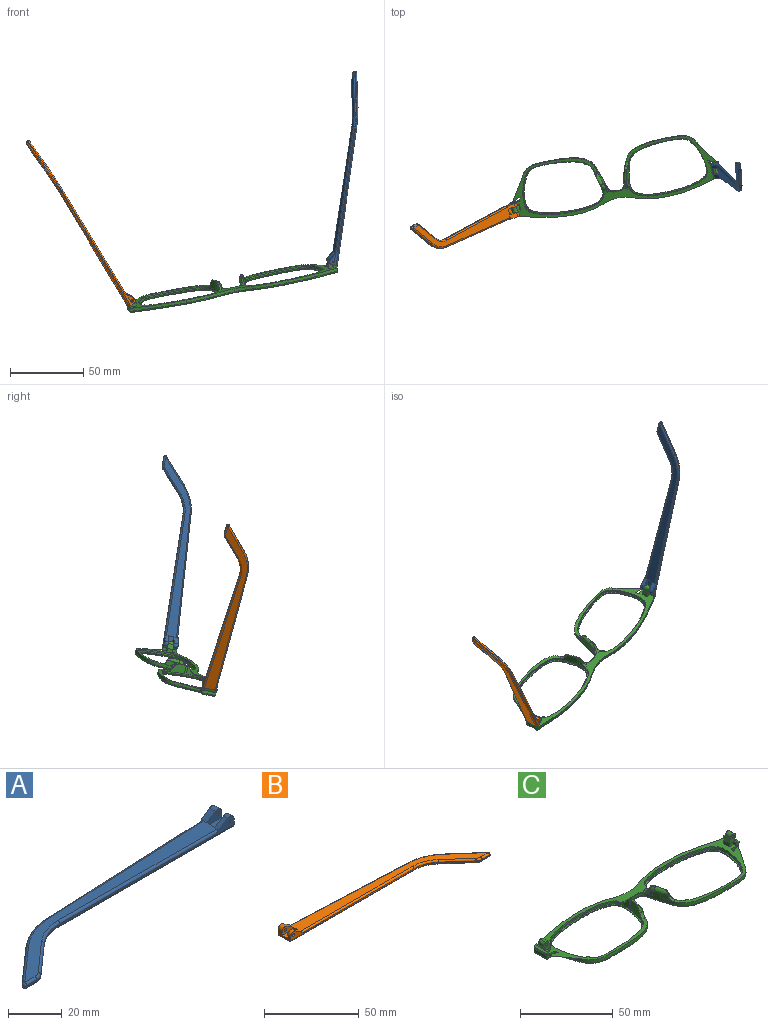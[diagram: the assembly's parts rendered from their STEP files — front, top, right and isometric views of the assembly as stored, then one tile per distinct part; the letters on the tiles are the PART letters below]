
ASSEMBLY  parts=3 mates=2
PART A: 43 faces, bbox 130.2x29.5x5.9 mm
  f0: plane 9.62x3.72mm, normal (1,0,0), area 24.7mm2, adj f1,f3,f4,f5,f10,f16,f18,f28
  f1: cylinder r=2.2mm len=3.45mm, axis (0,-1,0), area 11mm2, adj f0,f2,f4,f37
  f2: plane 6.01x3.91mm, normal (-0.55,0,0.84), area 12.7mm2, adj f1,f4,f9,f19,f37
  f3: plane 2.26x0.1mm, normal (0,0,1), area 0.1mm2, adj f0,f5,f18
  f4: plane 92.1x4.9mm, normal (0,-1,0), area 79.9mm2, adj f0,f1,f2,f14,f19,f36,f42
  f5: plane 93.42x4.13mm, normal (-0.04,1,0), area 64.8mm2, adj f0,f3,f11,f15,f17,f27,f28
  f6: plane 17.82x15.72mm, normal (-0.66,0.75,0), area 14.3mm2, adj f11,f12,f25,f30
  f7: plane 5.46x0.6mm, normal (0,-1,0), area 3.3mm2, adj f12,f13,f23,f32
  f8: plane 14.99x13.23mm, normal (0.66,-0.75,0), area 12mm2, adj f13,f14,f21,f34
  f9: plane 121.18x26.73mm, normal (0,0,1), area 627.7mm2, adj f2,f17,f19,f20,f21,f22,f23,f25
  f10: plane 129.1x27.08mm, normal (0,0,-1), area 686.5mm2, adj f0,f28,f29,f30,f32,f33,f34,f35
  f11: cylinder r=30mm len=18.52mm, axis (0,0,-1), area 12.2mm2, adj f5,f6,f26,f29
  f12: cylinder r=1mm len=1.75mm, axis (0,0,-1), area 1.5mm2, adj f6,f7,f24,f31
  f13: cylinder r=5mm len=3.31mm, axis (0,0,-1), area 2.2mm2, adj f7,f8,f22,f33
  f14: cylinder r=20mm len=13.23mm, axis (0,0,1), area 8.7mm2, adj f4,f8,f20,f35
  f15: plane 5.66x0.25mm, normal (0,0,-1), area 0.7mm2, adj f5,f17,f18
  f16: cylinder r=2.2mm len=3.45mm, axis (0,-1,0), area 14.8mm2, adj f0,f17,f18,f38
  f17: plane 6.01x3.91mm, normal (-0.55,0,0.84), area 16.9mm2, adj f5,f9,f15,f16,f18,f27,f38
  f18: plane 7.92x3.3mm, normal (0,1,0), area 15.9mm2, adj f0,f3,f15,f16,f17,f41
  f19: cylinder r=1mm len=84.18mm, axis (-1,0,0), area 131.4mm2, adj f2,f4,f9,f20
  f20: torus R=21mm, axis (0,0,1), area 23.1mm2, adj f9,f14,f19,f21
  f21: cylinder r=1mm len=15.65mm, axis (-0.75,-0.66,0), area 31.4mm2, adj f8,f9,f20,f22
  f22: torus R=4mm, axis (0,0,1), area 5.3mm2, adj f9,f13,f21,f23
  f23: cylinder r=1mm len=5.46mm, axis (-1,0,0), area 8.6mm2, adj f7,f9,f22,f24
  f24: sphere r=1mm, area 2.4mm2, adj f12,f23,f25
  f25: cylinder r=1mm len=18.48mm, axis (0.75,0.66,0), area 37.3mm2, adj f6,f9,f24,f26
  f26: torus R=29mm, axis (0,0,1), area 31.6mm2, adj f9,f11,f25,f27
  f27: cylinder r=1mm len=85.5mm, axis (1,0.04,0), area 133.5mm2, adj f5,f9,f17,f26
  f28: cylinder r=1mm len=93.46mm, axis (-1,-0.04,0), area 146.9mm2, adj f0,f5,f10,f29
  f29: torus R=29mm, axis (0,0,1), area 31.6mm2, adj f10,f11,f28,f30
  f30: cylinder r=1mm len=18.48mm, axis (-0.75,-0.66,0), area 37.3mm2, adj f6,f10,f29,f31
  f31: sphere r=1mm, area 2.4mm2, adj f12,f30,f32
  f32: cylinder r=1mm len=5.46mm, axis (1,0,0), area 8.6mm2, adj f7,f10,f31,f33
  f33: torus R=4mm, axis (0,0,1), area 5.3mm2, adj f10,f13,f32,f34
  f34: cylinder r=1mm len=15.65mm, axis (0.75,0.66,0), area 31.4mm2, adj f8,f10,f33,f35
  f35: torus R=21mm, axis (0,0,1), area 23.1mm2, adj f10,f14,f34,f36
  f36: cylinder r=1mm len=92.1mm, axis (1,0,0), area 144.7mm2, adj f0,f4,f10,f35
  f37: plane 7.92x4.7mm, normal (0,1,0), area 27mm2, adj f0,f1,f2,f39,f40,f42
  f38: plane 7.92x4.7mm, normal (0,-1,0), area 27mm2, adj f0,f16,f17,f39,f40,f41
  f39: plane 7.92x4.1mm, normal (0,0,1), area 32.5mm2, adj f0,f37,f38,f40
  f40: plane 4.1x1.4mm, normal (1,0,0), area 5.7mm2, adj f9,f37,f38,f39
  f41: cylinder r=0.5mm len=3.1mm, axis (0,-1,0), area 9.7mm2, adj f18,f38
  f42: cylinder r=0.5mm len=2.3mm, axis (0,-1,0), area 7.2mm2, adj f4,f37
PART B: 43 faces, bbox 130.2x29.5x5.9 mm
  f0: plane 9.62x3.72mm, normal (-1,0,0), area 24.7mm2, adj f1,f3,f4,f5,f10,f16,f18,f28
  f1: cylinder r=2.2mm len=3.45mm, axis (0,-1,0), area 11mm2, adj f0,f2,f4,f37
  f2: plane 6.01x3.91mm, normal (0.55,0,0.84), area 12.7mm2, adj f1,f4,f9,f19,f37
  f3: plane 2.26x0.1mm, normal (0,0,1), area 0.1mm2, adj f0,f5,f18
  f4: plane 92.1x4.9mm, normal (0,-1,0), area 78.2mm2, adj f0,f1,f2,f14,f19,f36,f42
  f5: plane 93.42x4.13mm, normal (0.04,1,0), area 64.8mm2, adj f0,f3,f11,f15,f17,f27,f28
  f6: plane 17.82x15.72mm, normal (0.66,0.75,0), area 14.3mm2, adj f11,f12,f25,f30
  f7: plane 5.46x0.6mm, normal (0,-1,0), area 3.3mm2, adj f12,f13,f23,f32
  f8: plane 14.99x13.23mm, normal (-0.66,-0.75,0), area 12mm2, adj f13,f14,f21,f34
  f9: plane 121.18x26.73mm, normal (0,0,1), area 627.7mm2, adj f2,f17,f19,f20,f21,f22,f23,f25
  f10: plane 129.1x27.08mm, normal (0,0,-1), area 686.5mm2, adj f0,f28,f29,f30,f32,f33,f34,f35
  f11: cylinder r=30mm len=18.52mm, axis (0,0,-1), area 12.2mm2, adj f5,f6,f26,f29
  f12: cylinder r=1mm len=1.75mm, axis (0,0,-1), area 1.5mm2, adj f6,f7,f24,f31
  f13: cylinder r=5mm len=3.31mm, axis (0,0,-1), area 2.2mm2, adj f7,f8,f22,f33
  f14: cylinder r=20mm len=13.23mm, axis (0,0,1), area 8.7mm2, adj f4,f8,f20,f35
  f15: plane 5.66x0.25mm, normal (0,0,-1), area 0.7mm2, adj f5,f17,f18
  f16: cylinder r=2.2mm len=3.45mm, axis (0,-1,0), area 14.8mm2, adj f0,f17,f18,f38
  f17: plane 6.01x3.91mm, normal (0.55,0,0.84), area 16.9mm2, adj f5,f9,f15,f16,f18,f27,f38
  f18: plane 7.92x3.3mm, normal (0,1,0), area 14.3mm2, adj f0,f3,f15,f16,f17,f41
  f19: cylinder r=1mm len=84.18mm, axis (1,0,0), area 131.4mm2, adj f2,f4,f9,f20
  f20: torus R=21mm, axis (0,0,1), area 23.1mm2, adj f9,f14,f19,f21
  f21: cylinder r=1mm len=15.65mm, axis (0.75,-0.66,0), area 31.4mm2, adj f8,f9,f20,f22
  f22: torus R=4mm, axis (0,0,1), area 5.3mm2, adj f9,f13,f21,f23
  f23: cylinder r=1mm len=5.46mm, axis (1,0,0), area 8.6mm2, adj f7,f9,f22,f24
  f24: sphere r=1mm, area 2.4mm2, adj f12,f23,f25
  f25: cylinder r=1mm len=18.48mm, axis (-0.75,0.66,0), area 37.3mm2, adj f6,f9,f24,f26
  f26: torus R=29mm, axis (0,0,1), area 31.6mm2, adj f9,f11,f25,f27
  f27: cylinder r=1mm len=85.5mm, axis (-1,0.04,0), area 133.5mm2, adj f5,f9,f17,f26
  f28: cylinder r=1mm len=93.46mm, axis (1,-0.04,0), area 146.9mm2, adj f0,f5,f10,f29
  f29: torus R=29mm, axis (0,0,1), area 31.6mm2, adj f10,f11,f28,f30
  f30: cylinder r=1mm len=18.48mm, axis (0.75,-0.66,0), area 37.3mm2, adj f6,f10,f29,f31
  f31: sphere r=1mm, area 2.4mm2, adj f12,f30,f32
  f32: cylinder r=1mm len=5.46mm, axis (-1,0,0), area 8.6mm2, adj f7,f10,f31,f33
  f33: torus R=4mm, axis (0,0,1), area 5.3mm2, adj f10,f13,f32,f34
  f34: cylinder r=1mm len=15.65mm, axis (-0.75,0.66,0), area 31.4mm2, adj f8,f10,f33,f35
  f35: torus R=21mm, axis (0,0,1), area 23.1mm2, adj f10,f14,f34,f36
  f36: cylinder r=1mm len=92.1mm, axis (-1,0,0), area 144.7mm2, adj f0,f4,f10,f35
  f37: plane 7.92x4.7mm, normal (0,1,0), area 25.4mm2, adj f0,f1,f2,f39,f40,f42
  f38: plane 7.92x4.7mm, normal (0,-1,0), area 25.4mm2, adj f0,f16,f17,f39,f40,f41
  f39: plane 7.92x4.1mm, normal (0,0,1), area 32.5mm2, adj f0,f37,f38,f40
  f40: plane 4.1x1.4mm, normal (-1,0,0), area 5.7mm2, adj f9,f37,f38,f39
  f41: cylinder r=0.88mm len=3.1mm, axis (0,-1,0), area 17mm2, adj f18,f38
  f42: cylinder r=0.88mm len=2.3mm, axis (0,-1,0), area 12.6mm2, adj f4,f37
PART C: 118 faces, bbox 148.1x40.9x18 mm
  f0: bspline ~1.82x1.22mm, area 0.7mm2, adj f2,f7,f37,f52
  f1: plane 147.73x40.5mm, normal (0,0,1), area 772.9mm2, adj f4,f5,f6,f7,f8,f12,f20,f23
  f2: bspline ~5.39x4.93mm, area 12.7mm2, adj f0,f7,f37,f41,f43,f52,f53
  f3: plane 4.46x1.45mm, normal (0,0,1), area 0.1mm2, adj f7,f38
  f4: plane 1.23x0.04mm, normal (0,0,1), area 0mm2, adj f1,f7,f22
  f5: plane 6.97x5.07mm, normal (0,1,0), area 22.7mm2, adj f1,f20,f21,f25,f27,f28,f30,f31
  f6: plane 3.2x2.36mm, normal (0,-1,0), area 5.7mm2, adj f1,f20,f26,f29
  f7: extruded ~73.26x39.84mm, area 292.7mm2, adj f0,f1,f2,f3,f4,f8,f13,f14
  f8: extruded ~35.39x5.69mm, area 72.2mm2, adj f1,f7,f18,f67
  f9: plane 144.78x37.85mm, normal (0,0,-1), area 478.1mm2, adj f13,f15,f17,f18,f19,f71,f73,f75
  f10: plane 56.31x36.53mm, normal (0,0,1), area 124.8mm2, adj f11,f19
  f11: extruded ~55.63x36.1mm, area 160.7mm2, adj f10,f12
  f12: extruded ~55.63x36.1mm, area 220.4mm2, adj f1,f11,f39,f40,f41,f42,f43,f44
  f13: bspline ~73.27x30.39mm, area 161.7mm2, adj f7,f9,f14,f71
  f14: bspline ~1x1mm, area 0.8mm2, adj f7,f13,f15
  f15: bspline ~8.99x1.23mm, area 12.6mm2, adj f7,f9,f14,f16
  f16: bspline ~1.04x1mm, area 0.7mm2, adj f7,f15,f17
  f17: bspline ~45.86x8.59mm, area 59.8mm2, adj f7,f9,f16,f18
  f18: bspline ~37.01x6.7mm, area 56.6mm2, adj f8,f9,f17,f76
  f19: bspline ~56.15x36.68mm, area 237.6mm2, adj f9,f10
  f20: plane 4x2.36mm, normal (-1,0,0), area 9.5mm2, adj f1,f5,f6,f21
  f21: plane 4x0.02mm, normal (0.34,0,0.94), area 0.1mm2, adj f5,f20,f28
  f22: plane 2.76x2.53mm, normal (0,-1,0), area 3.9mm2, adj f4,f26,f27,f35,f56
  f23: plane 7.67x1.6mm, normal (0.94,0,-0.34), area 13mm2, adj f1,f35,f36,f56
  f24: plane 2.1x1.69mm, normal (0,1,0), area 2.8mm2, adj f1,f25,f27,f36,f56
  f25: plane 3.3x2.1mm, normal (-1,0,0), area 6.9mm2, adj f1,f5,f24,f27
  f26: plane 2.35x2.1mm, normal (-1,0,0), area 4.9mm2, adj f1,f6,f22,f27,f29
  f27: plane 9.65x1.24mm, normal (0,0,1), area 8.2mm2, adj f5,f22,f24,f25,f26,f29,f30,f56
  f28: plane 4x3.31mm, normal (-0.94,0,0.34), area 14.1mm2, adj f5,f21,f29,f32
  f29: plane 5.77x5.06mm, normal (0,-1,0), area 17mm2, adj f6,f26,f27,f28,f30,f31,f32,f33
  f30: plane 4x2.21mm, normal (0.94,0,-0.34), area 9.4mm2, adj f5,f27,f29,f33
  f31: plane 4x0.01mm, normal (0.34,0,0.94), area 0mm2, adj f5,f29,f32,f33
  f32: cylinder r=1.98mm len=4mm, axis (0,1,0), area 12.4mm2, adj f5,f28,f29,f31
  f33: cylinder r=1.98mm len=4mm, axis (0,-1,0), area 12.4mm2, adj f5,f29,f30,f31
  f34: cylinder r=0.88mm len=4mm, axis (0,-1,0), area 22mm2, adj f5,f29
  f35: cone r=1mm half-angle=20deg, axis (0,0,1), area 2.3mm2, adj f1,f22,f23,f56
  f36: cylinder r=1mm len=2.28mm, axis (-0.34,0,-0.94), area 3mm2, adj f1,f23,f24,f56
  f37: extruded ~3.67x3.11mm, area 5.9mm2, adj f0,f2,f7,f59
  f38: extruded ~4.44x3.32mm, area 15.1mm2, adj f3,f7,f42,f43,f55
  f39: extruded ~4.98x1.36mm, area 6.6mm2, adj f12,f41
  f40: plane 3.63x0.97mm, normal (0,0,1), area 0.3mm2, adj f12,f41,f43
  f41: bspline ~15.5x15.35mm, area 6.4mm2, adj f2,f12,f39,f40,f54
  f42: bspline ~7.26x7.26mm, area 6.3mm2, adj f12,f38,f43,f55
  f43: bspline ~10.29x4.84mm, area 21.4mm2, adj f2,f7,f12,f38,f40,f42
  f44: plane 2.88x1.51mm, normal (0,0,-1), area 1.8mm2, adj f12,f45
  f45: cylinder r=2.28mm len=2.86mm, axis (0,0,1), area 1.8mm2, adj f1,f12,f44,f54
  f46: plane 2.5x1.83mm, normal (0,0,-1), area 1.7mm2, adj f12,f47
  f47: cylinder r=2.28mm len=2.47mm, axis (0,0,1), area 1.7mm2, adj f1,f12,f46
  f48: plane 1.79x1.31mm, normal (0,0,-1), area 0.9mm2, adj f12,f49
  f49: cylinder r=1.3mm len=1.78mm, axis (0,0,1), area 1.3mm2, adj f1,f12,f48
  f50: plane 1.95x1.68mm, normal (0,0,-1), area 1.5mm2, adj f12,f51
  f51: cylinder r=1.3mm len=1.93mm, axis (0,0,1), area 1.5mm2, adj f1,f12,f50
  f52: bspline ~2.66x2.04mm, area 1.9mm2, adj f0,f2,f7,f53,f58
  f53: bspline ~3.55x3.47mm, area 3.7mm2, adj f1,f2,f52,f54,f58
  f54: bspline ~5.1x3.97mm, area 7.6mm2, adj f1,f12,f41,f45,f53
  f55: bspline ~3.7x3.66mm, area 7.8mm2, adj f1,f7,f12,f38,f42
  f56: plane 9.71x1.44mm, normal (0.34,0,0.94), area 13.9mm2, adj f22,f23,f24,f27,f35,f36
  f57: bspline ~6.38x2.14mm, area 2.6mm2, adj f1,f7,f58,f115
  f58: bspline ~2.1x1.46mm, area 0.6mm2, adj f7,f52,f53,f57
  f59: bspline ~5.24x1.75mm, area 0mm2, adj f7,f37
  f60: bspline ~2.19x1.4mm, area 0.7mm2, adj f61,f66,f95,f110
  f61: bspline ~6.1x4.93mm, area 12.6mm2, adj f60,f66,f95,f99,f101,f110,f111
  f62: plane 4.46x1.45mm, normal (0,0,1), area 0.1mm2, adj f66,f96
  f63: plane 1.23x0.04mm, normal (0,0,1), area 0mm2, adj f1,f66,f80
  f64: plane 6.97x5.07mm, normal (0,1,0), area 22.7mm2, adj f1,f78,f79,f83,f85,f86,f88,f89
  f65: plane 3.2x2.36mm, normal (0,-1,0), area 5.7mm2, adj f1,f78,f84,f87
  f66: extruded ~73.26x39.84mm, area 292.7mm2, adj f1,f7,f60,f61,f62,f63,f67,f71
  f67: extruded ~35.39x5.69mm, area 72.2mm2, adj f1,f8,f66,f76
  f68: plane 56.31x36.53mm, normal (0,0,1), area 124.8mm2, adj f69,f77
  f69: extruded ~55.63x36.1mm, area 160.7mm2, adj f68,f70
  f70: extruded ~55.63x36.1mm, area 220.4mm2, adj f1,f69,f97,f98,f99,f100,f101,f102
  f71: bspline ~73.83x30.39mm, area 161.7mm2, adj f9,f13,f66,f72
  f72: bspline ~1x1mm, area 0.8mm2, adj f66,f71,f73
  f73: bspline ~8.99x1.23mm, area 12.6mm2, adj f9,f66,f72,f74
  f74: bspline ~1.04x1mm, area 0.8mm2, adj f66,f73,f75
  f75: bspline ~45.86x8.59mm, area 59.8mm2, adj f9,f66,f74,f76
  f76: bspline ~37.01x6.7mm, area 56.6mm2, adj f9,f18,f67,f75
  f77: bspline ~56.15x36.68mm, area 237.6mm2, adj f9,f68
  f78: plane 4x2.36mm, normal (1,0,0), area 9.5mm2, adj f1,f64,f65,f79
  f79: plane 4x0.02mm, normal (-0.34,0,0.94), area 0.1mm2, adj f64,f78,f86
  f80: plane 2.76x2.53mm, normal (0,-1,0), area 3.9mm2, adj f63,f84,f85,f93,f114
  f81: plane 7.67x1.6mm, normal (-0.94,0,-0.34), area 13mm2, adj f1,f93,f94,f114
  f82: plane 2.1x1.69mm, normal (0,1,0), area 2.8mm2, adj f1,f83,f85,f94,f114
  f83: plane 3.3x2.1mm, normal (1,0,0), area 6.9mm2, adj f1,f64,f82,f85
  f84: plane 2.35x2.1mm, normal (1,0,0), area 4.9mm2, adj f1,f65,f80,f85,f87
  f85: plane 9.65x1.24mm, normal (0,0,1), area 8.2mm2, adj f64,f80,f82,f83,f84,f87,f88,f114
  f86: plane 4x3.31mm, normal (0.94,0,0.34), area 14.1mm2, adj f64,f79,f87,f90
  f87: plane 5.77x5.06mm, normal (0,-1,0), area 17mm2, adj f65,f84,f85,f86,f88,f89,f90,f91
  f88: plane 4x2.21mm, normal (-0.94,0,-0.34), area 9.4mm2, adj f64,f85,f87,f91
  f89: plane 4x0.01mm, normal (-0.34,0,0.94), area 0mm2, adj f64,f87,f90,f91
  f90: cylinder r=1.98mm len=4mm, axis (0,1,0), area 12.4mm2, adj f64,f86,f87,f89
  f91: cylinder r=1.98mm len=4mm, axis (0,-1,0), area 12.4mm2, adj f64,f87,f88,f89
  f92: cylinder r=0.88mm len=4mm, axis (0,-1,0), area 22mm2, adj f64,f87
  f93: cone r=1mm half-angle=20deg, axis (0,0,1), area 2.3mm2, adj f1,f80,f81,f114
  f94: cylinder r=1mm len=2.28mm, axis (0.34,0,-0.94), area 3mm2, adj f1,f81,f82,f114
  f95: extruded ~3.67x3.11mm, area 5.9mm2, adj f60,f61,f66,f117
  f96: extruded ~4.44x3.32mm, area 15.1mm2, adj f62,f66,f100,f101,f113
  f97: extruded ~4.98x1.36mm, area 6.6mm2, adj f70,f99
  f98: plane 3.63x0.97mm, normal (0,0,1), area 0.3mm2, adj f70,f99,f101
  f99: bspline ~15.5x15.35mm, area 6.4mm2, adj f61,f70,f97,f98,f112
  f100: bspline ~7.26x7.26mm, area 6.2mm2, adj f70,f96,f101,f113
  f101: bspline ~10.29x4.84mm, area 21.5mm2, adj f61,f66,f70,f96,f98,f100
  f102: plane 2.88x1.51mm, normal (0,0,-1), area 1.8mm2, adj f70,f103
  f103: cylinder r=2.28mm len=2.86mm, axis (0,0,1), area 1.8mm2, adj f1,f70,f102,f112
  f104: plane 2.5x1.83mm, normal (0,0,-1), area 1.7mm2, adj f70,f105
  f105: cylinder r=2.28mm len=2.47mm, axis (0,0,1), area 1.7mm2, adj f1,f70,f104
  f106: plane 1.79x1.31mm, normal (0,0,-1), area 0.9mm2, adj f70,f107
  f107: cylinder r=1.3mm len=1.78mm, axis (0,0,1), area 1.3mm2, adj f1,f70,f106
  f108: plane 1.95x1.68mm, normal (0,0,-1), area 1.5mm2, adj f70,f109
  f109: cylinder r=1.3mm len=1.93mm, axis (0,0,1), area 1.5mm2, adj f1,f70,f108
  f110: bspline ~2.65x2.03mm, area 1.9mm2, adj f60,f61,f66,f111,f116
  f111: bspline ~3.55x3.47mm, area 3.7mm2, adj f1,f61,f110,f112,f116
  f112: bspline ~4.88x3.94mm, area 7.6mm2, adj f1,f70,f99,f103,f111
  f113: bspline ~3.7x3.66mm, area 7.8mm2, adj f1,f66,f70,f96,f100
  f114: plane 9.71x1.44mm, normal (-0.34,0,0.94), area 13.9mm2, adj f80,f81,f82,f85,f93,f94
  f115: bspline ~6.38x2.14mm, area 2.6mm2, adj f1,f57,f66,f116
  f116: bspline ~2.1x1.46mm, area 0.6mm2, adj f66,f110,f111,f115
  f117: bspline ~5.24x1.75mm, area 0mm2, adj f66,f95
PLACE A rot(axis=(0.65,0.14,-0.74),177.2deg) t=(-19.4,18.56,51.07)mm
PLACE B rot(axis=(-0.49,0.03,-0.87),163.6deg) t=(-140.11,16.82,-88.28)mm
PLACE C rot(axis=(0.08,0.1,-0.99),168.1deg) t=(-98.28,10.3,-27.73)mm
MATE revolute A.f1 <-> C.f90  axis (-0.22,0.96,0.18) through (-29.95,18.47,-8.36)mm
MATE revolute B.f41 <-> C.f33  axis (-0.22,0.96,0.18) through (-166.94,-8.25,-35)mm
